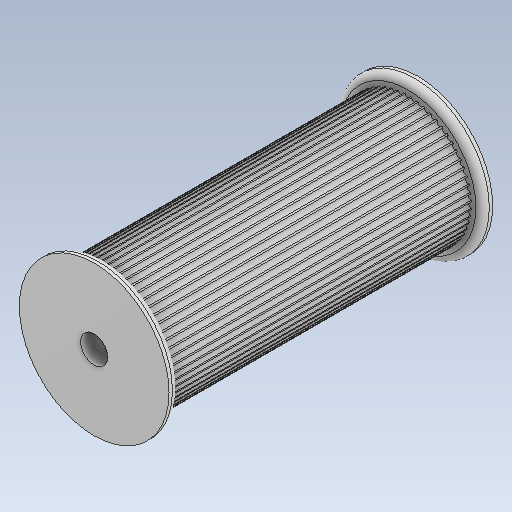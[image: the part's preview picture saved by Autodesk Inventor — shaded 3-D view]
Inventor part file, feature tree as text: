
AUTODESK INVENTOR PART (.ipt)
format: ipt  version: 2020 (Build 240168000, 168)  size: 330,752 bytes
history: mixed  units: in
note: dims shown in document units (in); Inventor stores cm internally (conversion verified against a paired STEP export)
features: fillet x1, imported_body x1
ambient origin geometry x8: Origin, YZ Plane, XZ Plane, XY Plane, X Axis, Y Axis, Z Axis, Center Point
bodies: Solid1 (imported_parasolid)
feature tree (2):
  fillet  "Fillet1"  [1 undecoded]
  imported_body  NMx_Import_Brep_tag  [imported B-rep: ~129 faces, bbox_mm=[44.4, 37.662953, 96.0]]
note: 1 required parameter value undecoded (feature->parameter linkage not recoverable at this tier; creation-order binding heuristic only, values carry confidence <= 0.55)
